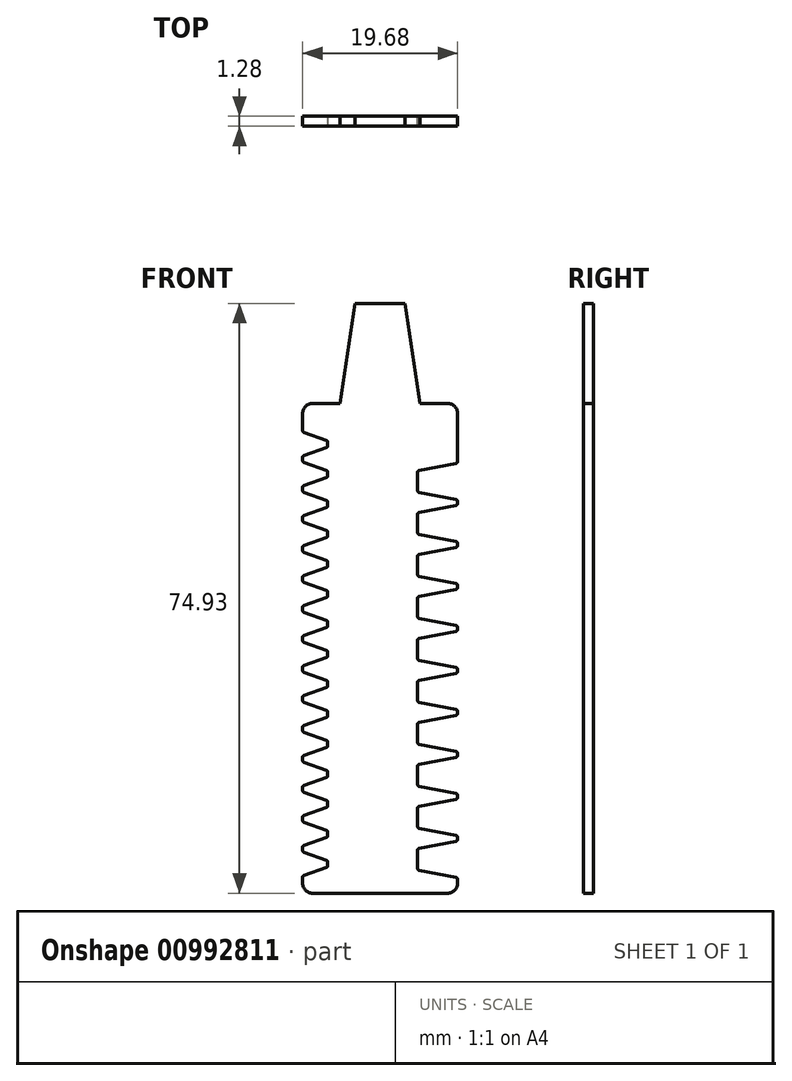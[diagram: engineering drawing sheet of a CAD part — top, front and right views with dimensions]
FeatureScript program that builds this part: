
annotation { "Feature Type Name" : "Feature", "Feature Type Description" : "" }
export const myFeature = defineFeature(function(context is Context, id is Id, definition is map)
    precondition{}
    {
        {
            var Q0;
            Q0=qCreatedBy(makeId("Front.planeOp"),FACE);
            var sketch = newSketch(context, id + "F0", { "sketchPlane" : qUnion([Q0])});
            skLineSegment(sketch, "E0", {"start": v(-9.84, -62.23) * mm, "end": v(0, -62.23) * mm});
            skLineSegment(sketch, "E1", {"start": v(0, -62.23) * mm, "end": v(9.84, -62.23) * mm});
            skLineSegment(sketch, "E2", {"start": v(9.84, -62.23) * mm, "end": v(9.84, -12.7) * mm});
            skLineSegment(sketch, "E3", {"start": v(9.84, 0) * mm, "end": v(0, 0) * mm});
            skLineSegment(sketch, "E4", {"start": v(-3.18, 0) * mm, "end": v(-3.18, 12.7) * mm});
            skLineSegment(sketch, "E5", {"start": v(-3.18, 12.7) * mm, "end": v(0, 12.7) * mm});
            skLineSegment(sketch, "E6", {"start": v(0, 12.7) * mm, "end": v(3.18, 12.7) * mm});
            skLineSegment(sketch, "E7", {"start": v(3.18, 12.7) * mm, "end": v(3.18, 0) * mm});
            skLineSegment(sketch, "E8", {"start": v(9.84, -12.7) * mm, "end": v(9.84, 0) * mm});
            skLineSegment(sketch, "E9", {"start": v(0, 0) * mm, "end": v(-9.84, 0) * mm});
            skLineSegment(sketch, "E10", {"start": v(-9.84, 0) * mm, "end": v(-9.84, -12.7) * mm});
            skLineSegment(sketch, "E11", {"start": v(-9.84, -12.7) * mm, "end": v(-9.84, -62.23) * mm});
            skLineSegment(sketch, "E12", {"start": v(-9.84, -12.7) * mm, "end": v(9.84, -12.7) * mm, "construction": true});
            skSolve(sketch);
        }
        {
            var Q0;
            Q0 = qSketchRegion(id + "F0", true);
            extrude(context, id + "F1", {"entities" : qUnion([Q0]), "endBound" : BoundingType.SYMMETRIC, "depth" : 1.27 * mm, "offsetDistance" : 25.4 * mm});
        }
        {
            var Q0;
            Q0=makeQuery(id+"F1.opExtrude","SWEPT_EDGE",EDGE,{"disambiguationData":[OSD([sQuery(id+"F0.wireOp",EDGE,"E10"),sQuery(id+"F0.wireOp",EDGE,"E11")])]});
            var Q1;
            Q1=makeQuery(id+"F1.opExtrude","SWEPT_EDGE",EDGE,{"disambiguationData":[OSD([sQuery(id+"F0.wireOp",EDGE,"E2"),sQuery(id+"F0.wireOp",EDGE,"E8")])]});
            fillet(context, id + "F2", {"entities" : qUnion([Q0, Q1]), "radius" : 1.27 * mm, "tangentPropagation" : true, "defaultsChanged" : true, "vertexSettings" : [], "allowEdgeOverflow" : false});
        }
        {
            var Q0;
            Q0=qCreatedBy(makeId("Front.planeOp"),FACE);
            var sketch = newSketch(context, id + "F3", { "sketchPlane" : qUnion([Q0])});
            skLineSegment(sketch, "E13", {"start": v(9.84, -55.37) * mm, "end": v(9.84, -60.45) * mm});
            skLineSegment(sketch, "E14", {"start": v(9.84, -60.45) * mm, "end": v(9.84, -57.91) * mm});
            skLineSegment(sketch, "E15", {"start": v(9.84, -57.91) * mm, "end": v(4.76, -57.91) * mm});
            skLineSegment(sketch, "E16", {"start": v(4.76, -57.91) * mm, "end": v(4.76, -56.77) * mm});
            skLineSegment(sketch, "E17", {"start": v(4.76, -57.91) * mm, "end": v(4.76, -59.06) * mm});
            skArc(sketch, "E18", {"start": v(4.97, -56.52) * mm, "mid": v(4.82, -56.6) * mm, "end": v(4.76, -56.77) * mm});
            skArc(sketch, "E19", {"start": v(4.76, -59.06) * mm, "mid": v(4.82, -59.22) * mm, "end": v(4.97, -59.3) * mm});
            skArc(sketch, "E20", {"start": v(9.84, -60.45) * mm, "mid": v(9.78, -60.3) * mm, "end": v(9.64, -60.2) * mm});
            skArc(sketch, "E21", {"start": v(9.64, -55.62) * mm, "mid": v(9.78, -55.54) * mm, "end": v(9.84, -55.37) * mm});
            skLineSegment(sketch, "E22", {"start": v(4.97, -56.52) * mm, "end": v(9.64, -55.62) * mm});
            skLineSegment(sketch, "E23", {"start": v(9.64, -60.2) * mm, "end": v(4.97, -59.3) * mm});
            skSolve(sketch);
        }
        {
            var Q0;
            Q0 = qSketchRegion(id + "F3", true);
            extrude(context, id + "F4", {"entities" : qUnion([Q0]), "operationType" : NewBodyOperationType.REMOVE, "endBound" : BoundingType.SYMMETRIC, "depth" : 25.4 * mm, "offsetDistance" : 25.4 * mm});
        }
        {
            var Q0;
            Q0=qCreatedBy(makeId("Front.planeOp"),FACE);
            var sketch = newSketch(context, id + "F5", { "sketchPlane" : qUnion([Q0])});
            skLineSegment(sketch, "E24.0", {"start": v(9.84, -55.37) * mm, "end": v(9.84, -60.45) * mm});
            skLineSegment(sketch, "E24.1", {"start": v(9.84, -60.45) * mm, "end": v(9.84, -57.91) * mm});
            skLineSegment(sketch, "E24.3", {"start": v(4.76, -57.91) * mm, "end": v(4.76, -56.77) * mm});
            skLineSegment(sketch, "E24.4", {"start": v(4.76, -57.91) * mm, "end": v(4.76, -59.06) * mm});
            skArc(sketch, "E24.5", {"start": v(4.97, -56.52) * mm, "mid": v(4.82, -56.6) * mm, "end": v(4.76, -56.77) * mm});
            skArc(sketch, "E24.6", {"start": v(4.76, -59.06) * mm, "mid": v(4.82, -59.22) * mm, "end": v(4.97, -59.3) * mm});
            skArc(sketch, "E24.7", {"start": v(9.84, -60.45) * mm, "mid": v(9.78, -60.3) * mm, "end": v(9.64, -60.2) * mm});
            skArc(sketch, "E24.8", {"start": v(9.64, -55.62) * mm, "mid": v(9.78, -55.54) * mm, "end": v(9.84, -55.37) * mm});
            skLineSegment(sketch, "E24.9", {"start": v(4.97, -56.52) * mm, "end": v(9.64, -55.62) * mm});
            skLineSegment(sketch, "E24.10", {"start": v(9.64, -60.2) * mm, "end": v(4.97, -59.3) * mm});
            skLineSegment(sketch, "E25.1.0.0", {"start": v(4.97, -51.19) * mm, "end": v(9.64, -50.3) * mm});
            skLineSegment(sketch, "E25.1.0.1", {"start": v(9.84, -50.04) * mm, "end": v(9.84, -55.12) * mm});
            skLineSegment(sketch, "E25.1.0.2", {"start": v(9.64, -54.87) * mm, "end": v(4.97, -53.98) * mm});
            skLineSegment(sketch, "E25.1.0.3", {"start": v(9.84, -55.12) * mm, "end": v(9.84, -52.58) * mm});
            skLineSegment(sketch, "E25.1.0.4", {"start": v(4.76, -52.58) * mm, "end": v(4.76, -53.73) * mm});
            skArc(sketch, "E25.1.0.5", {"start": v(4.97, -51.19) * mm, "mid": v(4.82, -51.27) * mm, "end": v(4.76, -51.44) * mm});
            skArc(sketch, "E25.1.0.6", {"start": v(4.76, -53.73) * mm, "mid": v(4.82, -53.89) * mm, "end": v(4.97, -53.98) * mm});
            skLineSegment(sketch, "E25.1.0.7", {"start": v(4.76, -52.58) * mm, "end": v(4.76, -51.44) * mm});
            skArc(sketch, "E25.1.0.8", {"start": v(9.64, -50.3) * mm, "mid": v(9.78, -50.2) * mm, "end": v(9.84, -50.04) * mm});
            skArc(sketch, "E25.1.0.9", {"start": v(9.84, -55.12) * mm, "mid": v(9.78, -54.96) * mm, "end": v(9.64, -54.87) * mm});
            skLineSegment(sketch, "E25.2.0.0", {"start": v(4.97, -45.85) * mm, "end": v(9.64, -44.96) * mm});
            skLineSegment(sketch, "E25.2.0.1", {"start": v(9.84, -44.7) * mm, "end": v(9.84, -49.79) * mm});
            skLineSegment(sketch, "E25.2.0.2", {"start": v(9.64, -49.54) * mm, "end": v(4.97, -48.64) * mm});
            skLineSegment(sketch, "E25.2.0.3", {"start": v(9.84, -49.79) * mm, "end": v(9.84, -47.25) * mm});
            skLineSegment(sketch, "E25.2.0.4", {"start": v(4.76, -47.25) * mm, "end": v(4.76, -48.4) * mm});
            skArc(sketch, "E25.2.0.5", {"start": v(4.97, -45.85) * mm, "mid": v(4.82, -45.94) * mm, "end": v(4.76, -46.1) * mm});
            skArc(sketch, "E25.2.0.6", {"start": v(4.76, -48.4) * mm, "mid": v(4.82, -48.55) * mm, "end": v(4.97, -48.64) * mm});
            skLineSegment(sketch, "E25.2.0.7", {"start": v(4.76, -47.25) * mm, "end": v(4.76, -46.1) * mm});
            skArc(sketch, "E25.2.0.8", {"start": v(9.64, -44.96) * mm, "mid": v(9.78, -44.87) * mm, "end": v(9.84, -44.7) * mm});
            skArc(sketch, "E25.2.0.9", {"start": v(9.84, -49.79) * mm, "mid": v(9.78, -49.62) * mm, "end": v(9.64, -49.54) * mm});
            skLineSegment(sketch, "E25.3.0.0", {"start": v(4.97, -40.52) * mm, "end": v(9.64, -39.62) * mm});
            skLineSegment(sketch, "E25.3.0.1", {"start": v(9.84, -39.37) * mm, "end": v(9.84, -44.45) * mm});
            skLineSegment(sketch, "E25.3.0.2", {"start": v(9.64, -44.2) * mm, "end": v(4.97, -43.3) * mm});
            skLineSegment(sketch, "E25.3.0.3", {"start": v(9.84, -44.45) * mm, "end": v(9.84, -41.91) * mm});
            skLineSegment(sketch, "E25.3.0.4", {"start": v(4.76, -41.91) * mm, "end": v(4.76, -43.06) * mm});
            skArc(sketch, "E25.3.0.5", {"start": v(4.97, -40.52) * mm, "mid": v(4.82, -40.6) * mm, "end": v(4.76, -40.77) * mm});
            skArc(sketch, "E25.3.0.6", {"start": v(4.76, -43.06) * mm, "mid": v(4.82, -43.22) * mm, "end": v(4.97, -43.3) * mm});
            skLineSegment(sketch, "E25.3.0.7", {"start": v(4.76, -41.91) * mm, "end": v(4.76, -40.77) * mm});
            skArc(sketch, "E25.3.0.8", {"start": v(9.64, -39.62) * mm, "mid": v(9.78, -39.53) * mm, "end": v(9.84, -39.37) * mm});
            skArc(sketch, "E25.3.0.9", {"start": v(9.84, -44.45) * mm, "mid": v(9.78, -44.3) * mm, "end": v(9.64, -44.2) * mm});
            skLineSegment(sketch, "E25.4.0.0", {"start": v(4.97, -35.18) * mm, "end": v(9.64, -34.29) * mm});
            skLineSegment(sketch, "E25.4.0.1", {"start": v(9.84, -34.04) * mm, "end": v(9.84, -39.12) * mm});
            skLineSegment(sketch, "E25.4.0.2", {"start": v(9.64, -38.87) * mm, "end": v(4.97, -37.97) * mm});
            skLineSegment(sketch, "E25.4.0.3", {"start": v(9.84, -39.12) * mm, "end": v(9.84, -36.58) * mm});
            skLineSegment(sketch, "E25.4.0.4", {"start": v(4.76, -36.58) * mm, "end": v(4.76, -37.72) * mm});
            skArc(sketch, "E25.4.0.5", {"start": v(4.97, -35.18) * mm, "mid": v(4.82, -35.27) * mm, "end": v(4.76, -35.43) * mm});
            skArc(sketch, "E25.4.0.6", {"start": v(4.76, -37.72) * mm, "mid": v(4.82, -37.89) * mm, "end": v(4.97, -37.97) * mm});
            skLineSegment(sketch, "E25.4.0.7", {"start": v(4.76, -36.58) * mm, "end": v(4.76, -35.43) * mm});
            skArc(sketch, "E25.4.0.8", {"start": v(9.64, -34.29) * mm, "mid": v(9.78, -34.2) * mm, "end": v(9.84, -34.04) * mm});
            skArc(sketch, "E25.4.0.9", {"start": v(9.84, -39.12) * mm, "mid": v(9.78, -38.96) * mm, "end": v(9.64, -38.87) * mm});
            skLineSegment(sketch, "E25.5.0.0", {"start": v(4.97, -29.85) * mm, "end": v(9.64, -28.95) * mm});
            skLineSegment(sketch, "E25.5.0.1", {"start": v(9.84, -28.7) * mm, "end": v(9.84, -33.78) * mm});
            skLineSegment(sketch, "E25.5.0.2", {"start": v(9.64, -33.54) * mm, "end": v(4.97, -32.64) * mm});
            skLineSegment(sketch, "E25.5.0.3", {"start": v(9.84, -33.78) * mm, "end": v(9.84, -31.24) * mm});
            skLineSegment(sketch, "E25.5.0.4", {"start": v(4.76, -31.24) * mm, "end": v(4.76, -32.39) * mm});
            skArc(sketch, "E25.5.0.5", {"start": v(4.97, -29.85) * mm, "mid": v(4.82, -29.94) * mm, "end": v(4.76, -30.1) * mm});
            skArc(sketch, "E25.5.0.6", {"start": v(4.76, -32.39) * mm, "mid": v(4.82, -32.55) * mm, "end": v(4.97, -32.64) * mm});
            skLineSegment(sketch, "E25.5.0.7", {"start": v(4.76, -31.24) * mm, "end": v(4.76, -30.1) * mm});
            skArc(sketch, "E25.5.0.8", {"start": v(9.64, -28.95) * mm, "mid": v(9.78, -28.87) * mm, "end": v(9.84, -28.7) * mm});
            skArc(sketch, "E25.5.0.9", {"start": v(9.84, -33.78) * mm, "mid": v(9.78, -33.62) * mm, "end": v(9.64, -33.54) * mm});
            skLineSegment(sketch, "E25.6.0.0", {"start": v(4.97, -24.52) * mm, "end": v(9.64, -23.62) * mm});
            skLineSegment(sketch, "E25.6.0.1", {"start": v(9.84, -23.37) * mm, "end": v(9.84, -28.45) * mm});
            skLineSegment(sketch, "E25.6.0.2", {"start": v(9.64, -28.2) * mm, "end": v(4.97, -27.3) * mm});
            skLineSegment(sketch, "E25.6.0.3", {"start": v(9.84, -28.45) * mm, "end": v(9.84, -25.91) * mm});
            skLineSegment(sketch, "E25.6.0.4", {"start": v(4.76, -25.91) * mm, "end": v(4.76, -27.06) * mm});
            skArc(sketch, "E25.6.0.5", {"start": v(4.97, -24.52) * mm, "mid": v(4.82, -24.6) * mm, "end": v(4.76, -24.77) * mm});
            skArc(sketch, "E25.6.0.6", {"start": v(4.76, -27.06) * mm, "mid": v(4.82, -27.22) * mm, "end": v(4.97, -27.3) * mm});
            skLineSegment(sketch, "E25.6.0.7", {"start": v(4.76, -25.91) * mm, "end": v(4.76, -24.77) * mm});
            skArc(sketch, "E25.6.0.8", {"start": v(9.64, -23.62) * mm, "mid": v(9.78, -23.53) * mm, "end": v(9.84, -23.37) * mm});
            skArc(sketch, "E25.6.0.9", {"start": v(9.84, -28.45) * mm, "mid": v(9.78, -28.29) * mm, "end": v(9.64, -28.2) * mm});
            skLineSegment(sketch, "E25.7.0.0", {"start": v(4.97, -19.18) * mm, "end": v(9.64, -18.29) * mm});
            skLineSegment(sketch, "E25.7.0.1", {"start": v(9.84, -18.04) * mm, "end": v(9.84, -23.12) * mm});
            skLineSegment(sketch, "E25.7.0.2", {"start": v(9.64, -22.87) * mm, "end": v(4.97, -21.97) * mm});
            skLineSegment(sketch, "E25.7.0.3", {"start": v(9.84, -23.12) * mm, "end": v(9.84, -20.58) * mm});
            skLineSegment(sketch, "E25.7.0.4", {"start": v(4.76, -20.58) * mm, "end": v(4.76, -21.72) * mm});
            skArc(sketch, "E25.7.0.5", {"start": v(4.97, -19.18) * mm, "mid": v(4.82, -19.27) * mm, "end": v(4.76, -19.43) * mm});
            skArc(sketch, "E25.7.0.6", {"start": v(4.76, -21.72) * mm, "mid": v(4.82, -21.88) * mm, "end": v(4.97, -21.97) * mm});
            skLineSegment(sketch, "E25.7.0.7", {"start": v(4.76, -20.58) * mm, "end": v(4.76, -19.43) * mm});
            skArc(sketch, "E25.7.0.8", {"start": v(9.64, -18.29) * mm, "mid": v(9.78, -18.2) * mm, "end": v(9.84, -18.04) * mm});
            skArc(sketch, "E25.7.0.9", {"start": v(9.84, -23.12) * mm, "mid": v(9.78, -22.95) * mm, "end": v(9.64, -22.87) * mm});
            skLineSegment(sketch, "E25.8.0.0", {"start": v(4.97, -13.85) * mm, "end": v(9.64, -12.95) * mm});
            skLineSegment(sketch, "E25.8.0.1", {"start": v(9.84, -12.7) * mm, "end": v(9.84, -17.78) * mm});
            skLineSegment(sketch, "E25.8.0.2", {"start": v(9.64, -17.53) * mm, "end": v(4.97, -16.64) * mm});
            skLineSegment(sketch, "E25.8.0.3", {"start": v(9.84, -17.78) * mm, "end": v(9.84, -15.24) * mm});
            skLineSegment(sketch, "E25.8.0.4", {"start": v(4.76, -15.24) * mm, "end": v(4.76, -16.39) * mm});
            skArc(sketch, "E25.8.0.5", {"start": v(4.97, -13.85) * mm, "mid": v(4.82, -13.94) * mm, "end": v(4.76, -14.1) * mm});
            skArc(sketch, "E25.8.0.6", {"start": v(4.76, -16.39) * mm, "mid": v(4.82, -16.55) * mm, "end": v(4.97, -16.64) * mm});
            skLineSegment(sketch, "E25.8.0.7", {"start": v(4.76, -15.24) * mm, "end": v(4.76, -14.1) * mm});
            skArc(sketch, "E25.8.0.8", {"start": v(9.64, -12.95) * mm, "mid": v(9.78, -12.86) * mm, "end": v(9.84, -12.7) * mm});
            skArc(sketch, "E25.8.0.9", {"start": v(9.84, -17.78) * mm, "mid": v(9.78, -17.62) * mm, "end": v(9.64, -17.53) * mm});
            skLineSegment(sketch, "E25.9.0.0", {"start": v(4.97, -8.51) * mm, "end": v(9.64, -7.62) * mm});
            skLineSegment(sketch, "E25.9.0.1", {"start": v(9.84, -7.37) * mm, "end": v(9.84, -12.45) * mm});
            skLineSegment(sketch, "E25.9.0.2", {"start": v(9.64, -12.2) * mm, "end": v(4.97, -11.3) * mm});
            skLineSegment(sketch, "E25.9.0.3", {"start": v(9.84, -12.45) * mm, "end": v(9.84, -9.9) * mm});
            skLineSegment(sketch, "E25.9.0.4", {"start": v(4.76, -9.9) * mm, "end": v(4.76, -11.05) * mm});
            skArc(sketch, "E25.9.0.5", {"start": v(4.97, -8.51) * mm, "mid": v(4.82, -8.6) * mm, "end": v(4.76, -8.76) * mm});
            skArc(sketch, "E25.9.0.6", {"start": v(4.76, -11.05) * mm, "mid": v(4.82, -11.22) * mm, "end": v(4.97, -11.3) * mm});
            skLineSegment(sketch, "E25.9.0.7", {"start": v(4.76, -9.9) * mm, "end": v(4.76, -8.76) * mm});
            skArc(sketch, "E25.9.0.8", {"start": v(9.64, -7.62) * mm, "mid": v(9.78, -7.53) * mm, "end": v(9.84, -7.37) * mm});
            skArc(sketch, "E25.9.0.9", {"start": v(9.84, -12.45) * mm, "mid": v(9.78, -12.29) * mm, "end": v(9.64, -12.2) * mm});
            skLineSegment(sketch, "E25.direction1", {"start": v(4.97, -59.3) * mm, "end": v(4.97, -53.98) * mm, "construction": true});
            skSolve(sketch);
        }
        {
            var Q0;
            Q0 = qSketchRegion(id + "F5", true);
            extrude(context, id + "F6", {"entities" : qUnion([Q0]), "operationType" : NewBodyOperationType.REMOVE, "endBound" : BoundingType.SYMMETRIC, "oppositeDirection" : true, "depth" : 25.4 * mm, "offsetDistance" : 25.4 * mm});
        }
        {
            var Q0;
            Q0=qCreatedBy(makeId("Front.planeOp"),FACE);
            var sketch = newSketch(context, id + "F7", { "sketchPlane" : qUnion([Q0])});
            skLineSegment(sketch, "E26", {"start": v(-5.08, 0) * mm, "end": v(-3.18, 12.7) * mm});
            skLineSegment(sketch, "E27", {"start": v(-3.18, 12.7) * mm, "end": v(3.18, 12.7) * mm});
            skLineSegment(sketch, "E28", {"start": v(3.18, 12.7) * mm, "end": v(5.08, 0) * mm});
            skLineSegment(sketch, "E29", {"start": v(5.08, 0) * mm, "end": v(0, 0) * mm});
            skLineSegment(sketch, "E30", {"start": v(0, 0) * mm, "end": v(-5.08, 0) * mm});
            skSolve(sketch);
        }
        {
            var Q0;
            Q0 = qSketchRegion(id + "F7", true);
            extrude(context, id + "F8", {"entities" : qUnion([Q0]), "operationType" : NewBodyOperationType.ADD, "endBound" : BoundingType.SYMMETRIC, "depth" : 1.27 * mm, "offsetDistance" : 25.4 * mm});
        }
        {
            var Q0;
            Q0=qCreatedBy(makeId("Front.planeOp"),FACE);
            var sketch = newSketch(context, id + "F9", { "sketchPlane" : qUnion([Q0])});
            skLineSegment(sketch, "E31", {"start": v(-9.84, -60.2) * mm, "end": v(-9.84, -56.77) * mm});
            skArc(sketch, "E32", {"start": v(-9.67, -59.96) * mm, "mid": v(-9.8, -60.05) * mm, "end": v(-9.84, -60.2) * mm});
            skArc(sketch, "E33", {"start": v(-9.84, -56.77) * mm, "mid": v(-9.8, -56.92) * mm, "end": v(-9.67, -57) * mm});
            skLineSegment(sketch, "E34", {"start": v(-9.67, -57) * mm, "end": v(-6.8, -58.04) * mm});
            skLineSegment(sketch, "E35", {"start": v(-6.8, -58.04) * mm, "end": v(-6.8, -58.93) * mm, "construction": true});
            skLineSegment(sketch, "E36", {"start": v(-6.8, -58.93) * mm, "end": v(-9.67, -59.96) * mm});
            skArc(sketch, "E37", {"start": v(-6.67, -58.22) * mm, "mid": v(-6.7, -58.1) * mm, "end": v(-6.8, -58.04) * mm});
            skArc(sketch, "E38", {"start": v(-6.8, -58.93) * mm, "mid": v(-6.7, -58.86) * mm, "end": v(-6.67, -58.75) * mm});
            skLineSegment(sketch, "E39", {"start": v(-6.67, -58.22) * mm, "end": v(-6.67, -58.75) * mm});
            skLineSegment(sketch, "E40", {"start": v(-9.84, -58.48) * mm, "end": v(-6.8, -58.48) * mm, "construction": true});
            skLineSegment(sketch, "E41", {"start": v(-9.84, -60.2) * mm, "end": v(-9.84, -62.23) * mm, "construction": true});
            skLineSegment(sketch, "E42", {"start": v(-8.57, -62.23) * mm, "end": v(-9.84, -62.23) * mm, "construction": true});
            skSolve(sketch);
        }
        {
            var Q0;
            Q0=qCreatedBy(makeId("Front.planeOp"),FACE);
            var sketch = newSketch(context, id + "F10", { "sketchPlane" : qUnion([Q0])});
            skLineSegment(sketch, "E43.0", {"start": v(-9.84, -60.2) * mm, "end": v(-9.84, -56.77) * mm});
            skArc(sketch, "E44.0", {"start": v(-9.84, -56.77) * mm, "mid": v(-9.8, -56.92) * mm, "end": v(-9.67, -57) * mm});
            skLineSegment(sketch, "E45.0", {"start": v(-9.67, -57) * mm, "end": v(-6.8, -58.04) * mm});
            skArc(sketch, "E46.0", {"start": v(-6.67, -58.22) * mm, "mid": v(-6.7, -58.1) * mm, "end": v(-6.8, -58.04) * mm});
            skLineSegment(sketch, "E47.0", {"start": v(-6.67, -58.22) * mm, "end": v(-6.67, -58.75) * mm});
            skArc(sketch, "E48.0", {"start": v(-6.8, -58.93) * mm, "mid": v(-6.7, -58.86) * mm, "end": v(-6.67, -58.75) * mm});
            skLineSegment(sketch, "E49.0", {"start": v(-6.8, -58.93) * mm, "end": v(-9.67, -59.96) * mm});
            skArc(sketch, "E50.0", {"start": v(-9.67, -59.96) * mm, "mid": v(-9.8, -60.05) * mm, "end": v(-9.84, -60.2) * mm});
            skLineSegment(sketch, "E51.1.0.0", {"start": v(-9.84, -56.39) * mm, "end": v(-9.84, -52.96) * mm});
            skLineSegment(sketch, "E51.1.0.1", {"start": v(-9.67, -53.2) * mm, "end": v(-6.8, -54.23) * mm});
            skLineSegment(sketch, "E51.1.0.2", {"start": v(-6.8, -55.12) * mm, "end": v(-9.67, -56.15) * mm});
            skArc(sketch, "E51.1.0.3", {"start": v(-9.84, -52.96) * mm, "mid": v(-9.8, -53.1) * mm, "end": v(-9.67, -53.2) * mm});
            skArc(sketch, "E51.1.0.4", {"start": v(-9.67, -56.15) * mm, "mid": v(-9.8, -56.24) * mm, "end": v(-9.84, -56.39) * mm});
            skLineSegment(sketch, "E51.1.0.5", {"start": v(-6.67, -54.4) * mm, "end": v(-6.67, -54.94) * mm});
            skArc(sketch, "E51.1.0.6", {"start": v(-6.67, -54.4) * mm, "mid": v(-6.7, -54.3) * mm, "end": v(-6.8, -54.23) * mm});
            skArc(sketch, "E51.1.0.7", {"start": v(-6.8, -55.12) * mm, "mid": v(-6.7, -55.05) * mm, "end": v(-6.67, -54.94) * mm});
            skLineSegment(sketch, "E51.2.0.0", {"start": v(-9.84, -52.58) * mm, "end": v(-9.84, -49.15) * mm});
            skLineSegment(sketch, "E51.2.0.1", {"start": v(-9.67, -49.39) * mm, "end": v(-6.8, -50.42) * mm});
            skLineSegment(sketch, "E51.2.0.2", {"start": v(-6.8, -51.3) * mm, "end": v(-9.67, -52.34) * mm});
            skArc(sketch, "E51.2.0.3", {"start": v(-9.84, -49.15) * mm, "mid": v(-9.8, -49.3) * mm, "end": v(-9.67, -49.39) * mm});
            skArc(sketch, "E51.2.0.4", {"start": v(-9.67, -52.34) * mm, "mid": v(-9.8, -52.43) * mm, "end": v(-9.84, -52.58) * mm});
            skLineSegment(sketch, "E51.2.0.5", {"start": v(-6.67, -50.6) * mm, "end": v(-6.67, -51.13) * mm});
            skArc(sketch, "E51.2.0.6", {"start": v(-6.67, -50.6) * mm, "mid": v(-6.7, -50.49) * mm, "end": v(-6.8, -50.42) * mm});
            skArc(sketch, "E51.2.0.7", {"start": v(-6.8, -51.3) * mm, "mid": v(-6.7, -51.24) * mm, "end": v(-6.67, -51.13) * mm});
            skLineSegment(sketch, "E51.direction1", {"start": v(-9.84, -60.2) * mm, "end": v(-9.84, -56.39) * mm, "construction": true});
            skLineSegment(sketch, "E52.0.3.0", {"start": v(-9.84, -48.77) * mm, "end": v(-9.84, -45.34) * mm});
            skLineSegment(sketch, "E52.3.3.0", {"start": v(-9.67, -45.58) * mm, "end": v(-6.8, -46.6) * mm});
            skLineSegment(sketch, "E52.6.3.0", {"start": v(-6.8, -47.5) * mm, "end": v(-9.67, -48.53) * mm});
            skArc(sketch, "E52.9.3.0", {"start": v(-9.84, -45.34) * mm, "mid": v(-9.8, -45.49) * mm, "end": v(-9.67, -45.58) * mm});
            skArc(sketch, "E52.13.3.0", {"start": v(-9.67, -48.53) * mm, "mid": v(-9.8, -48.62) * mm, "end": v(-9.84, -48.77) * mm});
            skLineSegment(sketch, "E52.17.3.0", {"start": v(-6.67, -46.79) * mm, "end": v(-6.67, -47.32) * mm});
            skArc(sketch, "E52.20.3.0", {"start": v(-6.67, -46.79) * mm, "mid": v(-6.7, -46.68) * mm, "end": v(-6.8, -46.6) * mm});
            skArc(sketch, "E52.24.3.0", {"start": v(-6.8, -47.5) * mm, "mid": v(-6.7, -47.43) * mm, "end": v(-6.67, -47.32) * mm});
            skLineSegment(sketch, "E52.0.4.0", {"start": v(-9.84, -44.96) * mm, "end": v(-9.84, -41.53) * mm});
            skLineSegment(sketch, "E52.3.4.0", {"start": v(-9.67, -41.77) * mm, "end": v(-6.8, -42.8) * mm});
            skLineSegment(sketch, "E52.6.4.0", {"start": v(-6.8, -43.69) * mm, "end": v(-9.67, -44.72) * mm});
            skArc(sketch, "E52.9.4.0", {"start": v(-9.84, -41.53) * mm, "mid": v(-9.8, -41.68) * mm, "end": v(-9.67, -41.77) * mm});
            skArc(sketch, "E52.13.4.0", {"start": v(-9.67, -44.72) * mm, "mid": v(-9.8, -44.81) * mm, "end": v(-9.84, -44.96) * mm});
            skLineSegment(sketch, "E52.17.4.0", {"start": v(-6.67, -42.98) * mm, "end": v(-6.67, -43.5) * mm});
            skArc(sketch, "E52.20.4.0", {"start": v(-6.67, -42.98) * mm, "mid": v(-6.7, -42.87) * mm, "end": v(-6.8, -42.8) * mm});
            skArc(sketch, "E52.24.4.0", {"start": v(-6.8, -43.69) * mm, "mid": v(-6.7, -43.62) * mm, "end": v(-6.67, -43.5) * mm});
            skLineSegment(sketch, "E52.0.5.0", {"start": v(-9.84, -41.15) * mm, "end": v(-9.84, -37.72) * mm});
            skLineSegment(sketch, "E52.3.5.0", {"start": v(-9.67, -37.96) * mm, "end": v(-6.8, -38.99) * mm});
            skLineSegment(sketch, "E52.6.5.0", {"start": v(-6.8, -39.88) * mm, "end": v(-9.67, -40.9) * mm});
            skArc(sketch, "E52.9.5.0", {"start": v(-9.84, -37.72) * mm, "mid": v(-9.8, -37.87) * mm, "end": v(-9.67, -37.96) * mm});
            skArc(sketch, "E52.13.5.0", {"start": v(-9.67, -40.9) * mm, "mid": v(-9.8, -41) * mm, "end": v(-9.84, -41.15) * mm});
            skLineSegment(sketch, "E52.17.5.0", {"start": v(-6.67, -39.17) * mm, "end": v(-6.67, -39.7) * mm});
            skArc(sketch, "E52.20.5.0", {"start": v(-6.67, -39.17) * mm, "mid": v(-6.7, -39.06) * mm, "end": v(-6.8, -38.99) * mm});
            skArc(sketch, "E52.24.5.0", {"start": v(-6.8, -39.88) * mm, "mid": v(-6.7, -39.8) * mm, "end": v(-6.67, -39.7) * mm});
            skLineSegment(sketch, "E52.0.6.0", {"start": v(-9.84, -37.34) * mm, "end": v(-9.84, -33.9) * mm});
            skLineSegment(sketch, "E52.3.6.0", {"start": v(-9.67, -34.15) * mm, "end": v(-6.8, -35.18) * mm});
            skLineSegment(sketch, "E52.6.6.0", {"start": v(-6.8, -36.07) * mm, "end": v(-9.67, -37.1) * mm});
            skArc(sketch, "E52.9.6.0", {"start": v(-9.84, -33.9) * mm, "mid": v(-9.8, -34.06) * mm, "end": v(-9.67, -34.15) * mm});
            skArc(sketch, "E52.13.6.0", {"start": v(-9.67, -37.1) * mm, "mid": v(-9.8, -37.2) * mm, "end": v(-9.84, -37.34) * mm});
            skLineSegment(sketch, "E52.17.6.0", {"start": v(-6.67, -35.36) * mm, "end": v(-6.67, -35.89) * mm});
            skArc(sketch, "E52.20.6.0", {"start": v(-6.67, -35.36) * mm, "mid": v(-6.7, -35.25) * mm, "end": v(-6.8, -35.18) * mm});
            skArc(sketch, "E52.24.6.0", {"start": v(-6.8, -36.07) * mm, "mid": v(-6.7, -36) * mm, "end": v(-6.67, -35.89) * mm});
            skLineSegment(sketch, "E52.0.7.0", {"start": v(-9.84, -33.53) * mm, "end": v(-9.84, -30.1) * mm});
            skLineSegment(sketch, "E52.3.7.0", {"start": v(-9.67, -30.34) * mm, "end": v(-6.8, -31.37) * mm});
            skLineSegment(sketch, "E52.6.7.0", {"start": v(-6.8, -32.26) * mm, "end": v(-9.67, -33.29) * mm});
            skArc(sketch, "E52.9.7.0", {"start": v(-9.84, -30.1) * mm, "mid": v(-9.8, -30.25) * mm, "end": v(-9.67, -30.34) * mm});
            skArc(sketch, "E52.13.7.0", {"start": v(-9.67, -33.29) * mm, "mid": v(-9.8, -33.38) * mm, "end": v(-9.84, -33.53) * mm});
            skLineSegment(sketch, "E52.17.7.0", {"start": v(-6.67, -31.55) * mm, "end": v(-6.67, -32.08) * mm});
            skArc(sketch, "E52.20.7.0", {"start": v(-6.67, -31.55) * mm, "mid": v(-6.7, -31.44) * mm, "end": v(-6.8, -31.37) * mm});
            skArc(sketch, "E52.24.7.0", {"start": v(-6.8, -32.26) * mm, "mid": v(-6.7, -32.19) * mm, "end": v(-6.67, -32.08) * mm});
            skLineSegment(sketch, "E52.0.8.0", {"start": v(-9.84, -29.72) * mm, "end": v(-9.84, -26.29) * mm});
            skLineSegment(sketch, "E52.3.8.0", {"start": v(-9.67, -26.53) * mm, "end": v(-6.8, -27.56) * mm});
            skLineSegment(sketch, "E52.6.8.0", {"start": v(-6.8, -28.45) * mm, "end": v(-9.67, -29.48) * mm});
            skArc(sketch, "E52.9.8.0", {"start": v(-9.84, -26.29) * mm, "mid": v(-9.8, -26.44) * mm, "end": v(-9.67, -26.53) * mm});
            skArc(sketch, "E52.13.8.0", {"start": v(-9.67, -29.48) * mm, "mid": v(-9.8, -29.57) * mm, "end": v(-9.84, -29.72) * mm});
            skLineSegment(sketch, "E52.17.8.0", {"start": v(-6.67, -27.74) * mm, "end": v(-6.67, -28.27) * mm});
            skArc(sketch, "E52.20.8.0", {"start": v(-6.67, -27.74) * mm, "mid": v(-6.7, -27.63) * mm, "end": v(-6.8, -27.56) * mm});
            skArc(sketch, "E52.24.8.0", {"start": v(-6.8, -28.45) * mm, "mid": v(-6.7, -28.38) * mm, "end": v(-6.67, -28.27) * mm});
            skLineSegment(sketch, "E53.0.9.0", {"start": v(-9.84, -25.9) * mm, "end": v(-9.84, -22.48) * mm});
            skLineSegment(sketch, "E53.3.9.0", {"start": v(-9.67, -22.72) * mm, "end": v(-6.8, -23.75) * mm});
            skLineSegment(sketch, "E53.6.9.0", {"start": v(-6.8, -24.64) * mm, "end": v(-9.67, -25.67) * mm});
            skArc(sketch, "E53.9.9.0", {"start": v(-9.84, -22.48) * mm, "mid": v(-9.8, -22.63) * mm, "end": v(-9.67, -22.72) * mm});
            skArc(sketch, "E53.13.9.0", {"start": v(-9.67, -25.67) * mm, "mid": v(-9.8, -25.76) * mm, "end": v(-9.84, -25.9) * mm});
            skLineSegment(sketch, "E53.17.9.0", {"start": v(-6.67, -23.93) * mm, "end": v(-6.67, -24.46) * mm});
            skArc(sketch, "E53.20.9.0", {"start": v(-6.67, -23.93) * mm, "mid": v(-6.7, -23.82) * mm, "end": v(-6.8, -23.75) * mm});
            skArc(sketch, "E53.24.9.0", {"start": v(-6.8, -24.64) * mm, "mid": v(-6.7, -24.57) * mm, "end": v(-6.67, -24.46) * mm});
            skLineSegment(sketch, "E53.0.10.0", {"start": v(-9.84, -22.1) * mm, "end": v(-9.84, -18.67) * mm});
            skLineSegment(sketch, "E53.3.10.0", {"start": v(-9.67, -18.9) * mm, "end": v(-6.8, -19.94) * mm});
            skLineSegment(sketch, "E53.6.10.0", {"start": v(-6.8, -20.83) * mm, "end": v(-9.67, -21.86) * mm});
            skArc(sketch, "E53.9.10.0", {"start": v(-9.84, -18.67) * mm, "mid": v(-9.8, -18.82) * mm, "end": v(-9.67, -18.9) * mm});
            skArc(sketch, "E53.13.10.0", {"start": v(-9.67, -21.86) * mm, "mid": v(-9.8, -21.95) * mm, "end": v(-9.84, -22.1) * mm});
            skLineSegment(sketch, "E53.17.10.0", {"start": v(-6.67, -20.12) * mm, "end": v(-6.67, -20.65) * mm});
            skArc(sketch, "E53.20.10.0", {"start": v(-6.67, -20.12) * mm, "mid": v(-6.7, -20) * mm, "end": v(-6.8, -19.94) * mm});
            skArc(sketch, "E53.24.10.0", {"start": v(-6.8, -20.83) * mm, "mid": v(-6.7, -20.76) * mm, "end": v(-6.67, -20.65) * mm});
            skLineSegment(sketch, "E53.0.11.0", {"start": v(-9.84, -18.29) * mm, "end": v(-9.84, -14.86) * mm});
            skLineSegment(sketch, "E53.3.11.0", {"start": v(-9.67, -15.1) * mm, "end": v(-6.8, -16.13) * mm});
            skLineSegment(sketch, "E53.6.11.0", {"start": v(-6.8, -17.02) * mm, "end": v(-9.67, -18.05) * mm});
            skArc(sketch, "E53.9.11.0", {"start": v(-9.84, -14.86) * mm, "mid": v(-9.8, -15) * mm, "end": v(-9.67, -15.1) * mm});
            skArc(sketch, "E53.13.11.0", {"start": v(-9.67, -18.05) * mm, "mid": v(-9.8, -18.14) * mm, "end": v(-9.84, -18.29) * mm});
            skLineSegment(sketch, "E53.17.11.0", {"start": v(-6.67, -16.3) * mm, "end": v(-6.67, -16.84) * mm});
            skArc(sketch, "E53.20.11.0", {"start": v(-6.67, -16.3) * mm, "mid": v(-6.7, -16.2) * mm, "end": v(-6.8, -16.13) * mm});
            skArc(sketch, "E53.24.11.0", {"start": v(-6.8, -17.02) * mm, "mid": v(-6.7, -16.95) * mm, "end": v(-6.67, -16.84) * mm});
            skLineSegment(sketch, "E54.0.12.0", {"start": v(-9.84, -14.48) * mm, "end": v(-9.84, -11.05) * mm});
            skLineSegment(sketch, "E54.3.12.0", {"start": v(-9.67, -11.29) * mm, "end": v(-6.8, -12.32) * mm});
            skLineSegment(sketch, "E54.6.12.0", {"start": v(-6.8, -13.2) * mm, "end": v(-9.67, -14.24) * mm});
            skArc(sketch, "E54.9.12.0", {"start": v(-9.84, -11.05) * mm, "mid": v(-9.8, -11.2) * mm, "end": v(-9.67, -11.29) * mm});
            skArc(sketch, "E54.13.12.0", {"start": v(-9.67, -14.24) * mm, "mid": v(-9.8, -14.33) * mm, "end": v(-9.84, -14.48) * mm});
            skLineSegment(sketch, "E54.17.12.0", {"start": v(-6.67, -12.5) * mm, "end": v(-6.67, -13.03) * mm});
            skArc(sketch, "E54.20.12.0", {"start": v(-6.67, -12.5) * mm, "mid": v(-6.7, -12.39) * mm, "end": v(-6.8, -12.32) * mm});
            skArc(sketch, "E54.24.12.0", {"start": v(-6.8, -13.2) * mm, "mid": v(-6.7, -13.14) * mm, "end": v(-6.67, -13.03) * mm});
            skLineSegment(sketch, "E54.0.13.0", {"start": v(-9.84, -10.67) * mm, "end": v(-9.84, -7.24) * mm});
            skLineSegment(sketch, "E54.3.13.0", {"start": v(-9.67, -7.48) * mm, "end": v(-6.8, -8.5) * mm});
            skLineSegment(sketch, "E54.6.13.0", {"start": v(-6.8, -9.4) * mm, "end": v(-9.67, -10.43) * mm});
            skArc(sketch, "E54.9.13.0", {"start": v(-9.84, -7.24) * mm, "mid": v(-9.8, -7.39) * mm, "end": v(-9.67, -7.48) * mm});
            skArc(sketch, "E54.13.13.0", {"start": v(-9.67, -10.43) * mm, "mid": v(-9.8, -10.52) * mm, "end": v(-9.84, -10.67) * mm});
            skLineSegment(sketch, "E54.17.13.0", {"start": v(-6.67, -8.69) * mm, "end": v(-6.67, -9.22) * mm});
            skArc(sketch, "E54.20.13.0", {"start": v(-6.67, -8.69) * mm, "mid": v(-6.7, -8.58) * mm, "end": v(-6.8, -8.5) * mm});
            skArc(sketch, "E54.24.13.0", {"start": v(-6.8, -9.4) * mm, "mid": v(-6.7, -9.33) * mm, "end": v(-6.67, -9.22) * mm});
            skLineSegment(sketch, "E54.0.14.0", {"start": v(-9.84, -6.86) * mm, "end": v(-9.84, -3.43) * mm});
            skLineSegment(sketch, "E54.3.14.0", {"start": v(-9.67, -3.67) * mm, "end": v(-6.8, -4.7) * mm});
            skLineSegment(sketch, "E54.6.14.0", {"start": v(-6.8, -5.59) * mm, "end": v(-9.67, -6.62) * mm});
            skArc(sketch, "E54.9.14.0", {"start": v(-9.84, -3.43) * mm, "mid": v(-9.8, -3.58) * mm, "end": v(-9.67, -3.67) * mm});
            skArc(sketch, "E54.13.14.0", {"start": v(-9.67, -6.62) * mm, "mid": v(-9.8, -6.71) * mm, "end": v(-9.84, -6.86) * mm});
            skLineSegment(sketch, "E54.17.14.0", {"start": v(-6.67, -4.88) * mm, "end": v(-6.67, -5.4) * mm});
            skArc(sketch, "E54.20.14.0", {"start": v(-6.67, -4.88) * mm, "mid": v(-6.7, -4.77) * mm, "end": v(-6.8, -4.7) * mm});
            skArc(sketch, "E54.24.14.0", {"start": v(-6.8, -5.59) * mm, "mid": v(-6.7, -5.52) * mm, "end": v(-6.67, -5.4) * mm});
            skSolve(sketch);
        }
        {
            var Q0;
            Q0 = qSketchRegion(id + "F10", true);
            extrude(context, id + "F11", {"entities" : qUnion([Q0]), "operationType" : NewBodyOperationType.REMOVE, "endBound" : BoundingType.SYMMETRIC, "oppositeDirection" : true, "depth" : 25.4 * mm, "offsetDistance" : 25.4 * mm});
        }
    });
